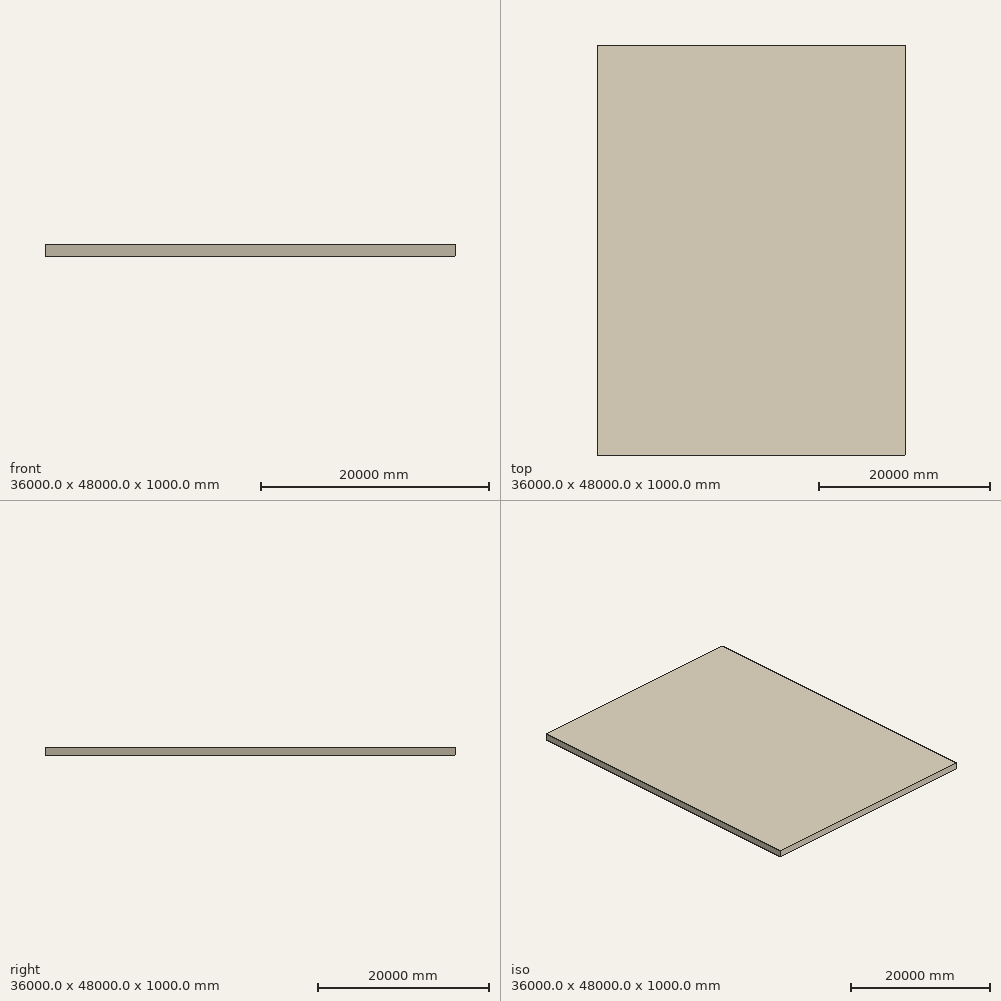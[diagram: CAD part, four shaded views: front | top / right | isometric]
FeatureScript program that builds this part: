
annotation { "Feature Type Name" : "Feature", "Feature Type Description" : "" }
export const myFeature = defineFeature(function(context is Context, id is Id, definition is map)
    precondition{}
    {
        {
            var Q0;
            Q0=qCreatedBy(makeId("Top.planeOp"),FACE);
            var sketch = newSketch(context, id + "F0", { "sketchPlane" : qUnion([Q0])});
            skLineSegment(sketch, "E0.bottom", {"start": v(0, 0) * mm, "end": v(36000, 0) * mm});
            skLineSegment(sketch, "E0.top", {"start": v(0, 48000) * mm, "end": v(36000, 48000) * mm});
            skLineSegment(sketch, "E0.left", {"start": v(0, 0) * mm, "end": v(0, 48000) * mm});
            skLineSegment(sketch, "E0.right", {"start": v(36000, 0) * mm, "end": v(36000, 48000) * mm});
            skSolve(sketch);
        }
        {
            var Q0;
            Q0=makeQuery(id+"F0.imprint","IMPRINT",FACE,{"disambiguationData":[TD([[makeQuery(id+"F0.imprint","IMPRINT",EDGE,{"derivedFrom":sQuery(id+"F0.wireOp",EDGE,"E0.bottom")}),1.0]])]});
            extrude(context, id + "F1", {"entities" : qUnion([Q0]), "depth" : 1000 * mm});
        }
    });
